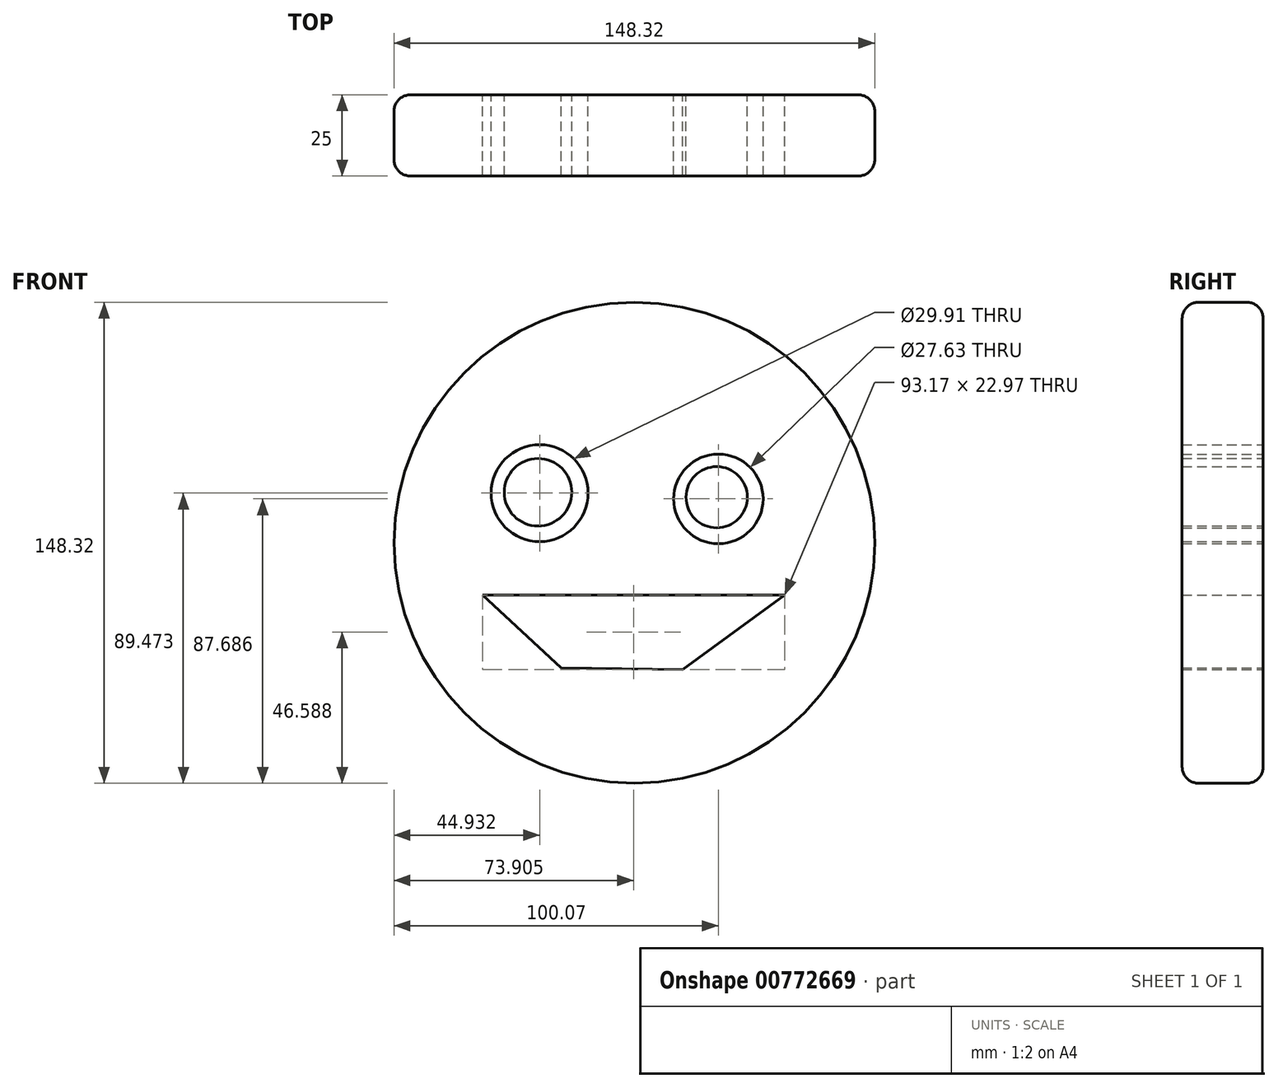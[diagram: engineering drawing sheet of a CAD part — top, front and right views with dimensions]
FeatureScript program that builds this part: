
annotation { "Feature Type Name" : "Feature", "Feature Type Description" : "" }
export const myFeature = defineFeature(function(context is Context, id is Id, definition is map)
    precondition{}
    {
        {
            var Q0;
            Q0=qCreatedBy(makeId("Front.planeOp"),FACE);
            var sketch = newSketch(context, id + "F0", { "sketchPlane" : qUnion([Q0])});
            skCircle(sketch, "E0", {"center": v(0, 0) * mm, "radius": 74.16 * mm});
            skCircle(sketch, "E1", {"center": v(-29.23, 15.31) * mm, "radius": 14.96 * mm});
            skCircle(sketch, "E2", {"center": v(25.9, 13.53) * mm, "radius": 13.82 * mm});
            skLineSegment(sketch, "E3", {"start": v(-46.84, -16.08) * mm, "end": v(46.33, -16.08) * mm});
            skLineSegment(sketch, "E4", {"start": v(-46.84, -16.08) * mm, "end": v(-22.6, -38.55) * mm});
            skLineSegment(sketch, "E5", {"start": v(46.33, -16.08) * mm, "end": v(14.93, -39.06) * mm});
            skLineSegment(sketch, "E6", {"start": v(14.93, -39.06) * mm, "end": v(-22.6, -38.55) * mm});
            skSolve(sketch);
        }
        {
            var Q0;
            Q0 = qSketchRegion(id + "F0", true);
            extrude(context, id + "F1", {"entities" : qUnion([Q0]), "depth" : 25 * mm, "offsetDistance" : 25 * mm});
        }
        {
            var Q0;
            Q0=qCreatedBy(makeId("Front.planeOp"),FACE);
            var sketch = newSketch(context, id + "F2", { "sketchPlane" : qUnion([Q0])});
            skCircle(sketch, "E7", {"center": v(-29.74, 15.57) * mm, "radius": 10.41 * mm});
            skCircle(sketch, "E8", {"center": v(25.4, 14.04) * mm, "radius": 9.44 * mm});
            skSolve(sketch);
        }
        {
            var Q0;
            Q0=makeQuery(id+"F2.imprint","IMPRINT",FACE,{"disambiguationData":[TD([[makeQuery(id+"F2.imprint","IMPRINT",EDGE,{"derivedFrom":sQuery(id+"F2.wireOp",EDGE,"E8")}),1.0]])]});
            var Q1;
            Q1=makeQuery(id+"F2.imprint","IMPRINT",FACE,{"disambiguationData":[TD([[makeQuery(id+"F2.imprint","IMPRINT",EDGE,{"derivedFrom":sQuery(id+"F2.wireOp",EDGE,"E7")}),1.0]])]});
            extrude(context, id + "F3", {"entities" : qUnion([Q0, Q1]), "depth" : 25 * mm, "offsetDistance" : 25 * mm});
        }
        {
            var Q0;
            Q0=makeQuery(id+"F1.opExtrude","SWEPT_FACE",FACE,{"disambiguationData":[OSD([sQuery(id+"F0.wireOp",EDGE,"E0")])]});
            fillet(context, id + "F4", {"entities" : qUnion([Q0]), "radius" : 5 * mm, "tangentPropagation" : true, "allowEdgeOverflow" : false});
        }
    });
